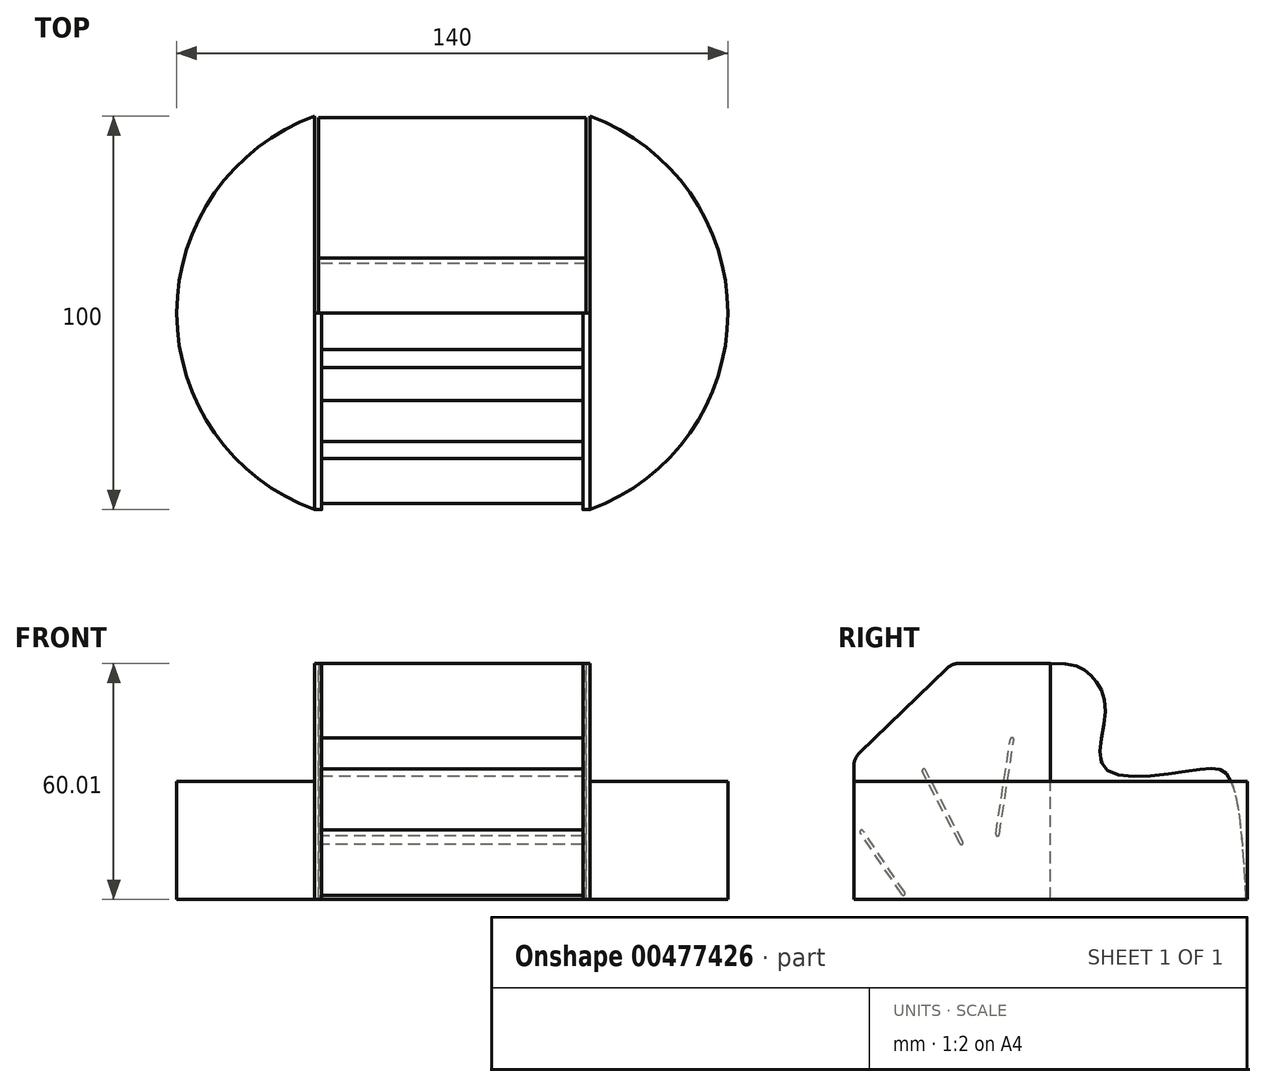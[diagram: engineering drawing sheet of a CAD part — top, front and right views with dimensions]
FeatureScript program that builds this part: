
annotation { "Feature Type Name" : "Feature", "Feature Type Description" : "" }
export const myFeature = defineFeature(function(context is Context, id is Id, definition is map)
    precondition{}
    {
        {
            var Q0;
            Q0=qCreatedBy(makeId("Top.planeOp"),FACE);
            var sketch = newSketch(context, id + "F0", { "sketchPlane" : qUnion([Q0])});
            skLineSegment(sketch, "E0.bottom", {"start": v(-35, 50) * mm, "end": v(35, 50) * mm});
            skLineSegment(sketch, "E0.top", {"start": v(-35, -50) * mm, "end": v(35, -50) * mm});
            skLineSegment(sketch, "E0.left", {"start": v(-35, 50) * mm, "end": v(-35, -50) * mm});
            skLineSegment(sketch, "E0.right", {"start": v(35, 50) * mm, "end": v(35, -50) * mm});
            skPoint(sketch, "E0.middle", {"position": v(0, 0) * mm});
            skArc(sketch, "E1", {"start": v(-35, 50) * mm, "mid": v(-70, 0) * mm, "end": v(-35, -50) * mm});
            skPoint(sketch, "E2.endSnap0", {"position": v(-70, 0) * mm});
            skArc(sketch, "E3.MirrorCS", {"start": v(35, 50) * mm, "mid": v(70, 0) * mm, "end": v(35, -50) * mm});
            skSolve(sketch);
        }
        {
            var Q0;
            Q0=makeQuery(id+"F0.imprint","IMPRINT",FACE,{"disambiguationData":[TD([[makeQuery(id+"F0.imprint","IMPRINT",EDGE,{"derivedFrom":sQuery(id+"F0.wireOp",EDGE,"E0.left")}),-1.0]])]});
            var Q1;
            Q1=makeQuery(id+"F0.imprint","IMPRINT",FACE,{"disambiguationData":[TD([[makeQuery(id+"F0.imprint","IMPRINT",EDGE,{"derivedFrom":sQuery(id+"F0.wireOp",EDGE,"E0.right")}),1.0]])]});
            extrude(context, id + "F1", {"entities" : qUnion([Q0, Q1]), "depth" : 30 * mm, "offsetDistance" : 25 * mm});
        }
        {
            var Q0;
            Q0=qCreatedBy(makeId("Right.planeOp"),FACE);
            var sketch = newSketch(context, id + "F2", { "sketchPlane" : qUnion([Q0])});
            skLineSegment(sketch, "E4", {"start": v(0, 0) * mm, "end": v(0, 60) * mm});
            skFitSpline(sketch, "E5", {"points": [v(0, 60) * mm, v(10.33, 56.77) * mm, v(13.88, 48.11) * mm, v(13.8, 33.23) * mm, v(36.8, 32.9) * mm, v(44.91, 31.59) * mm, v(48.49, 15.66) * mm, v(49.56, 0) * mm], "startDerivative": vector(141.79, 3.41) * mm, "endDerivative": vector(4.65, -95.74) * mm});
            skLineSegment(sketch, "E6", {"start": v(0, 0) * mm, "end": v(49.56, 0) * mm});
            skSolve(sketch);
        }
        {
            var Q0;
            Q0 = qSketchRegion(id + "F2", true);
            var Q1;
            Q1=makeQuery(id+"F1.opExtrude","SWEPT_FACE",FACE,{"disambiguationData":[OSD([sQuery(id+"F0.wireOp",EDGE,"E0.right")])]});
            var Q2;
            Q2=makeQuery(id+"F1.opExtrude","SWEPT_FACE",FACE,{"disambiguationData":[OSD([sQuery(id+"F0.wireOp",EDGE,"E0.left")])]});
            extrude(context, id + "F3", {"entities" : qUnion([Q0]), "endBound" : BoundingType.UP_TO_SURFACE, "depth" : 53.8 * mm, "endBoundEntityFace" : qUnion([Q1]), "hasOffset" : true, "offsetDistance" : 1 * mm, "hasSecondDirection" : true, "secondDirectionBound" : SecondDirectionBoundingType.UP_TO_SURFACE, "secondDirectionOppositeDirection" : true, "secondDirectionDepth" : 25 * mm, "secondDirectionBoundEntityFace" : qUnion([Q2]), "hasSecondDirectionOffset" : true, "secondDirectionOffsetDistance" : 1 * mm});
        }
        {
            var Q0;
            Q0=makeQuery(id+"F1.opExtrude","SWEPT_FACE",FACE,{"disambiguationData":[OSD([sQuery(id+"F0.wireOp",EDGE,"E0.left")])]});
            var sketch = newSketch(context, id + "F4", { "sketchPlane" : qUnion([Q0])});
            skLineSegment(sketch, "E7", {"start": v(0, 0) * mm, "end": v(0, 60) * mm});
            skLineSegment(sketch, "E8", {"start": v(0, 60) * mm, "end": v(-22.98, 60) * mm});
            skLineSegment(sketch, "E9", {"start": v(-26.45, 58.6) * mm, "end": v(-48.48, 37.3) * mm});
            skLineSegment(sketch, "E10", {"start": v(-50, 33.7) * mm, "end": v(-50, 0) * mm});
            skLineSegment(sketch, "E11", {"start": v(-50, 0) * mm, "end": v(0, 0) * mm});
            skPoint(sketch, "E12.visualSharp", {"position": v(-25, 60) * mm});
            skArc(sketch, "E12.filletArc", {"start": v(-22.98, 60) * mm, "mid": v(-24.85, 59.64) * mm, "end": v(-26.45, 58.6) * mm});
            skPoint(sketch, "E13.visualSharp", {"position": v(-50, 35.82) * mm});
            skArc(sketch, "E13.filletArc", {"start": v(-48.48, 37.3) * mm, "mid": v(-49.6, 35.65) * mm, "end": v(-50, 33.7) * mm});
            skSolve(sketch);
        }
        {
            var Q0;
            Q0 = qSketchRegion(id + "F4", true);
            extrude(context, id + "F5", {"entities" : qUnion([Q0]), "depth" : 1.8 * mm, "offsetDistance" : 25 * mm});
        }
        {
            var Q0;
            Q0=makeQuery(id+"F5.opExtrude","SWEPT_BODY",BODY,{"disambiguationData":[OSD([sQuery(id+"F4.wireOp",EDGE,"E7"),sQuery(id+"F4.wireOp",EDGE,"E8"),sQuery(id+"F4.wireOp",EDGE,"E9"),sQuery(id+"F4.wireOp",EDGE,"E10"),sQuery(id+"F4.wireOp",EDGE,"E11"),sQuery(id+"F4.wireOp",EDGE,"E12.filletArc"),sQuery(id+"F4.wireOp",EDGE,"E13.filletArc")])]});
            var Q1;
            Q1=qCreatedBy(makeId("Right.planeOp"),FACE);
            mirror(context, id + "F6", {"entities" : qUnion([Q0]), "mirrorPlane" : qUnion([Q1])});
        }
        {
            var Q0;
            Q0=makeQuery(id+"F5.opExtrude","CAP_FACE",FACE,{"disambiguationData":[OSD([sQuery(id+"F4.wireOp",EDGE,"E7"),sQuery(id+"F4.wireOp",EDGE,"E8"),sQuery(id+"F4.wireOp",EDGE,"E9"),sQuery(id+"F4.wireOp",EDGE,"E10"),sQuery(id+"F4.wireOp",EDGE,"E11"),sQuery(id+"F4.wireOp",EDGE,"E12.filletArc"),sQuery(id+"F4.wireOp",EDGE,"E13.filletArc")])],"isStart":false});
            var sketch = newSketch(context, id + "F7", { "sketchPlane" : qUnion([Q0])});
            skLineSegment(sketch, "E14", {"start": v(-9.8, 40.63) * mm, "end": v(-13.48, 16.54) * mm, "construction": true});
            skLineSegment(sketch, "E15", {"start": v(-32.2, 32.65) * mm, "end": v(-22.69, 14.39) * mm, "construction": true});
            skLineSegment(sketch, "E16", {"start": v(-48, 17.15) * mm, "end": v(-37.42, 1.5) * mm, "construction": true});
            skArc(sketch, "E17.0.startCap", {"start": v(-32.6, 32.44) * mm, "mid": v(-32.4, 33.05) * mm, "end": v(-31.8, 32.86) * mm});
            skArc(sketch, "E17.0.endCap", {"start": v(-22.29, 14.6) * mm, "mid": v(-22.48, 14) * mm, "end": v(-23.09, 14.18) * mm});
            skLineSegment(sketch, "E17.0.left", {"start": v(-31.8, 32.86) * mm, "end": v(-22.29, 14.6) * mm});
            skLineSegment(sketch, "E17.0.right", {"start": v(-32.6, 32.44) * mm, "end": v(-23.09, 14.18) * mm});
            skArc(sketch, "E17.1.startCap", {"start": v(-48.38, 16.9) * mm, "mid": v(-48.26, 17.52) * mm, "end": v(-47.64, 17.4) * mm});
            skArc(sketch, "E17.1.endCap", {"start": v(-37.05, 1.75) * mm, "mid": v(-37.17, 1.13) * mm, "end": v(-37.8, 1.25) * mm});
            skLineSegment(sketch, "E17.1.left", {"start": v(-47.64, 17.4) * mm, "end": v(-37.05, 1.75) * mm});
            skLineSegment(sketch, "E17.1.right", {"start": v(-48.38, 16.9) * mm, "end": v(-37.8, 1.25) * mm});
            skArc(sketch, "E17.2.startCap", {"start": v(-10.24, 40.7) * mm, "mid": v(-9.73, 41.08) * mm, "end": v(-9.35, 40.56) * mm});
            skArc(sketch, "E17.2.endCap", {"start": v(-13.03, 16.47) * mm, "mid": v(-13.55, 16.1) * mm, "end": v(-13.92, 16.6) * mm});
            skLineSegment(sketch, "E17.2.left", {"start": v(-9.35, 40.56) * mm, "end": v(-13.03, 16.47) * mm});
            skLineSegment(sketch, "E17.2.right", {"start": v(-10.24, 40.7) * mm, "end": v(-13.92, 16.6) * mm});
            skSolve(sketch);
        }
        {
            var Q0;
            Q0 = qSketchRegion(id + "F7", true);
            var Q1;
            Q1=makeQuery(id+"F6.opPattern","COPY",FACE,{"derivedFrom":makeQuery(id+"F5.opExtrude","CAP_FACE",FACE,{"disambiguationData":[OSD([sQuery(id+"F4.wireOp",EDGE,"E7"),sQuery(id+"F4.wireOp",EDGE,"E8"),sQuery(id+"F4.wireOp",EDGE,"E9"),sQuery(id+"F4.wireOp",EDGE,"E10"),sQuery(id+"F4.wireOp",EDGE,"E11"),sQuery(id+"F4.wireOp",EDGE,"E12.filletArc"),sQuery(id+"F4.wireOp",EDGE,"E13.filletArc")])],"isStart":false}),"instanceName":"1"});
            extrude(context, id + "F8", {"entities" : qUnion([Q0]), "endBound" : BoundingType.UP_TO_SURFACE, "depth" : 25 * mm, "endBoundEntityFace" : qUnion([Q1]), "offsetDistance" : 25 * mm});
        }
    });
